# Revit family: Gira_216700
name_source: partatom
category: Electrical Fixtures
revit_build: Autodesk Revit 2017 (Build: 20160225_1515(x64)
units: mm (PartAtom-declared; Revit-internal decimal feet)

## family parameters
Cut with Voids When Loaded = No
Host = Face
Maintain Annotation Orientation = No
Part Type = Normal
Room Calculation Point = No
Round Connector Dimension = Use Diameter
Shared = No

## types (1)
- KNX IP router KNX DRA
    BIM = https://media.live.bim.site X1 REG KNX.rfa
    BIMSITE_PRODUCT_ID = ae5a2d61a97159a84ca3a2909b559f3bdc49fc3b
    Bus connection included = No
    Cost = 0 $
    Default Elevation = 1219 mm
    Description = IP router DRA KNX KNX IP router,DRA plus Features: - Connection of KNX lines with aid of data networks and use of the Internet protocol (IP). - Coupling of a KNX system together with the Gira HomeServer or Gira FacilityServer. - Filtering and forwarding of telegrams. - Use as line or area coupler. - Use as KNX clock. - Recording of KNX telegrams on a microSD card. - Hardware from index status I14 prepared for KNX Secure (additional firmware update required). - Up to four tunnelling connection possible simultaneously. - Reliable communication for automatic correction of telegram losses in WLAN (Reliable Communication).,Notes : - Supply via external DC 24 V. - The Gira Project Assistant (GPA) is required for firmware updates. The GPA is available free of charge in the Gira download area.
    GTIN = 4010337084440
    HAN = 216700
    HeinzeBIM = https://www.heinze.de
    Manufacturer = Gira
    Number of inputs = 0
    Radio frequent bidirectional = No
    Transparent = No
    URL = https://www.gira.de
    With label area = No

## geometry (parser evidence)
native form markers: Blend x2, Sweep x3
no freeform markers — native parametric forms only
